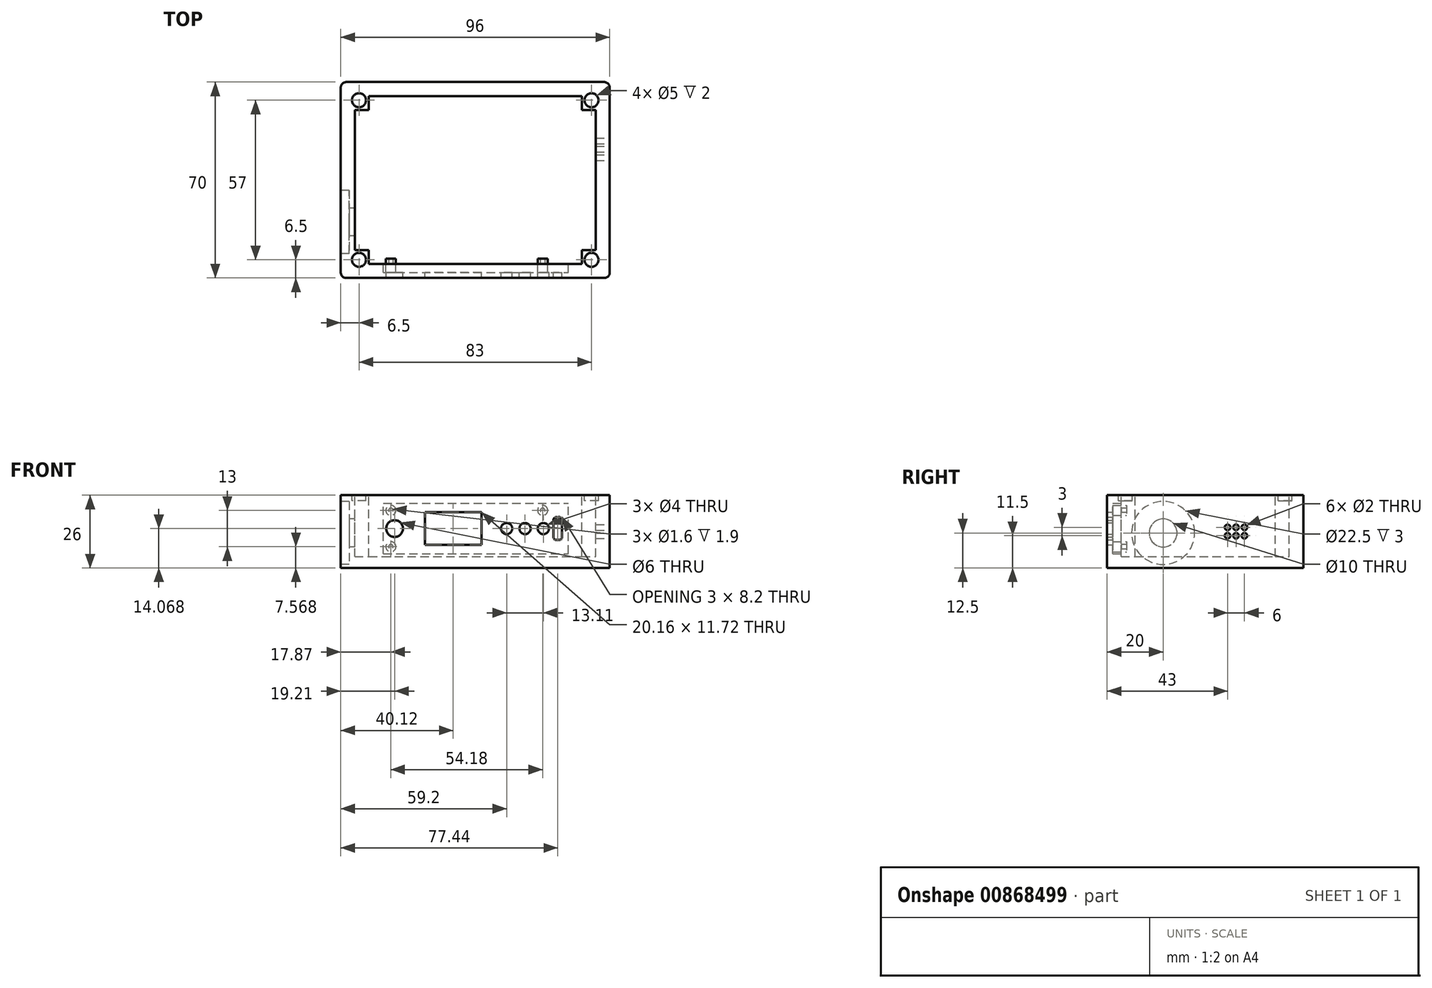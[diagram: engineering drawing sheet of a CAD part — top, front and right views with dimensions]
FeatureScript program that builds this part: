
annotation { "Feature Type Name" : "Feature", "Feature Type Description" : "" }
export const myFeature = defineFeature(function(context is Context, id is Id, definition is map)
    precondition{}
    {
        {
            var Q0;
            Q0=qCreatedBy(makeId("Top.planeOp"),FACE);
            var sketch = newSketch(context, id + "F0", { "sketchPlane" : qUnion([Q0])});
            skLineSegment(sketch, "E0.bottom", {"start": v(-46, 35) * mm, "end": v(46, 35) * mm});
            skLineSegment(sketch, "E0.top", {"start": v(-46, -35) * mm, "end": v(46, -35) * mm});
            skLineSegment(sketch, "E0.left", {"start": v(-48, 33) * mm, "end": v(-48, -33) * mm});
            skLineSegment(sketch, "E0.right", {"start": v(48, 33) * mm, "end": v(48, -33) * mm});
            skPoint(sketch, "E0.middle", {"position": v(0, 0) * mm});
            skPoint(sketch, "E1.visualSharp", {"position": v(-48, 35) * mm});
            skArc(sketch, "E1.filletArc", {"start": v(-46, 35) * mm, "mid": v(-47.41, 34.41) * mm, "end": v(-48, 33) * mm});
            skPoint(sketch, "E2.visualSharp", {"position": v(-48, -35) * mm});
            skArc(sketch, "E2.filletArc", {"start": v(-48, -33) * mm, "mid": v(-47.41, -34.41) * mm, "end": v(-46, -35) * mm});
            skPoint(sketch, "E3.visualSharp", {"position": v(48, -35) * mm});
            skArc(sketch, "E3.filletArc", {"start": v(46, -35) * mm, "mid": v(47.41, -34.41) * mm, "end": v(48, -33) * mm});
            skPoint(sketch, "E4.visualSharp", {"position": v(48, 35) * mm});
            skArc(sketch, "E4.filletArc", {"start": v(48, 33) * mm, "mid": v(47.41, 34.41) * mm, "end": v(46, 35) * mm});
            skSolve(sketch);
        }
        {
            var Q0;
            Q0=makeQuery(id+"F0.imprint","IMPRINT",FACE,{"disambiguationData":[TD([[makeQuery(id+"F0.imprint","IMPRINT",EDGE,{"derivedFrom":sQuery(id+"F0.wireOp",EDGE,"U18dfylj-Norm-gyCY-oxJm-QVkYRqjWbd2D.bottom")}),-1.0]])]});
            var Q1;
            Q1=qSketchRegion(id+"F0",true);
            extrude(context, id + "F1", {"entities" : qUnion([Q0, Q1]), "depth" : 26 * mm, "offsetDistance" : 25 * mm});
        }
        {
            var Q0;
            Q0=makeQuery(id+"F1.opExtrude","CAP_FACE",FACE,{"disambiguationData":[OSD([sQuery(id+"F0.wireOp",EDGE,"E0.bottom"),sQuery(id+"F0.wireOp",EDGE,"E0.top"),sQuery(id+"F0.wireOp",EDGE,"E0.left"),sQuery(id+"F0.wireOp",EDGE,"E0.right"),sQuery(id+"F0.wireOp",EDGE,"E1.filletArc"),sQuery(id+"F0.wireOp",EDGE,"E2.filletArc"),sQuery(id+"F0.wireOp",EDGE,"E3.filletArc"),sQuery(id+"F0.wireOp",EDGE,"E4.filletArc")])],"isStart":false});
            var sketch = newSketch(context, id + "F2", { "sketchPlane" : qUnion([Q0])});
            skLineSegment(sketch, "E5.bottom", {"start": v(-44.5, 33) * mm, "end": v(44.5, 33) * mm});
            skLineSegment(sketch, "E5.top", {"start": v(-44.5, -33) * mm, "end": v(44.5, -33) * mm});
            skLineSegment(sketch, "E5.left", {"start": v(-46, 31.5) * mm, "end": v(-46, -31.5) * mm});
            skLineSegment(sketch, "E5.right", {"start": v(46, 31.5) * mm, "end": v(46, -31.5) * mm});
            skPoint(sketch, "E5.middle", {"position": v(0, 0) * mm});
            skPoint(sketch, "E6.visualSharp", {"position": v(-46, 33) * mm});
            skArc(sketch, "E6.filletArc", {"start": v(-44.5, 33) * mm, "mid": v(-45.56, 32.56) * mm, "end": v(-46, 31.5) * mm});
            skPoint(sketch, "E7.visualSharp", {"position": v(46, 33) * mm});
            skArc(sketch, "E7.filletArc", {"start": v(46, 31.5) * mm, "mid": v(45.56, 32.56) * mm, "end": v(44.5, 33) * mm});
            skPoint(sketch, "E8.visualSharp", {"position": v(46, -33) * mm});
            skArc(sketch, "E8.filletArc", {"start": v(44.5, -33) * mm, "mid": v(45.56, -32.56) * mm, "end": v(46, -31.5) * mm});
            skPoint(sketch, "E9.visualSharp", {"position": v(-46, -33) * mm});
            skArc(sketch, "E9.filletArc", {"start": v(-46, -31.5) * mm, "mid": v(-45.56, -32.56) * mm, "end": v(-44.5, -33) * mm});
            skLineSegment(sketch, "E10.bottom", {"start": v(-44, 31.5) * mm, "end": v(44, 31.5) * mm});
            skLineSegment(sketch, "E10.top", {"start": v(-44, -31.5) * mm, "end": v(44, -31.5) * mm});
            skLineSegment(sketch, "E10.left", {"start": v(-44.5, 31) * mm, "end": v(-44.5, -31) * mm});
            skLineSegment(sketch, "E10.right", {"start": v(44.5, 31) * mm, "end": v(44.5, -31) * mm});
            skArc(sketch, "E11.filletArc", {"start": v(-44, 31.5) * mm, "mid": v(-44.35, 31.35) * mm, "end": v(-44.5, 31) * mm});
            skArc(sketch, "E12.filletArc", {"start": v(-44.5, -31) * mm, "mid": v(-44.35, -31.35) * mm, "end": v(-44, -31.5) * mm});
            skArc(sketch, "E13.filletArc", {"start": v(44, -31.5) * mm, "mid": v(44.35, -31.35) * mm, "end": v(44.5, -31) * mm});
            skArc(sketch, "E14.filletArc", {"start": v(44.5, 31) * mm, "mid": v(44.35, 31.35) * mm, "end": v(44, 31.5) * mm});
            skSolve(sketch);
        }
        {
            var Q0;
            Q0=makeQuery(id+"FVReVV0em28uw1l_1.boolean.opBoolean","SPLIT",FACE,{"disambiguationData":[TD([makeQuery(id+"FVReVV0em28uw1l_1.opExtrude","SWEPT_FACE",FACE,{"disambiguationData":[OSD([sQuery(id+"F2.wireOp",EDGE,"E10.bottom")])]})])],"derivedFrom":makeQuery(id+"F1.opExtrude","CAP_FACE",FACE,{"disambiguationData":[OSD([sQuery(id+"F0.wireOp",EDGE,"E0.bottom"),sQuery(id+"F0.wireOp",EDGE,"E0.top"),sQuery(id+"F0.wireOp",EDGE,"E0.left"),sQuery(id+"F0.wireOp",EDGE,"E0.right"),sQuery(id+"F0.wireOp",EDGE,"E1.filletArc"),sQuery(id+"F0.wireOp",EDGE,"E2.filletArc"),sQuery(id+"F0.wireOp",EDGE,"E3.filletArc"),sQuery(id+"F0.wireOp",EDGE,"E4.filletArc")])],"isStart":false})});
            var sketch = newSketch(context, id + "F3", { "sketchPlane" : qUnion([Q0])});
            skCircle(sketch, "E15", {"center": v(-41.5, -28.5) * mm, "radius": 2.5 * mm});
            skCircle(sketch, "E16", {"center": v(-41.5, 28.5) * mm, "radius": 2.5 * mm});
            skCircle(sketch, "E17", {"center": v(41.5, 28.5) * mm, "radius": 2.5 * mm});
            skCircle(sketch, "E18", {"center": v(41.5, -28.5) * mm, "radius": 2.5 * mm});
            skSolve(sketch);
        }
        {
            var Q0;
            Q0=makeQuery(id+"F3.imprint","IMPRINT",FACE,{"disambiguationData":[TD([[makeQuery(id+"F3.imprint","IMPRINT",EDGE,{"derivedFrom":sQuery(id+"F3.wireOp",EDGE,"E15")}),1.0]])]});
            var Q1;
            Q1=makeQuery(id+"F3.imprint","IMPRINT",FACE,{"disambiguationData":[TD([[makeQuery(id+"F3.imprint","IMPRINT",EDGE,{"derivedFrom":sQuery(id+"F3.wireOp",EDGE,"E16")}),1.0]])]});
            var Q2;
            Q2=makeQuery(id+"F3.imprint","IMPRINT",FACE,{"disambiguationData":[TD([[makeQuery(id+"F3.imprint","IMPRINT",EDGE,{"derivedFrom":sQuery(id+"F3.wireOp",EDGE,"E17")}),1.0]])]});
            var Q3;
            Q3=makeQuery(id+"F3.imprint","IMPRINT",FACE,{"disambiguationData":[TD([[makeQuery(id+"F3.imprint","IMPRINT",EDGE,{"derivedFrom":sQuery(id+"F3.wireOp",EDGE,"E18")}),1.0]])]});
            extrude(context, id + "F4", {"entities" : qUnion([Q0, Q1, Q2, Q3]), "operationType" : NewBodyOperationType.REMOVE, "oppositeDirection" : true, "depth" : 2 * mm, "offsetDistance" : 25 * mm});
        }
        {
            var Q0;
            Q0=makeQuery(id+"FVReVV0em28uw1l_1.boolean.opBoolean","SPLIT",FACE,{"disambiguationData":[TD([makeQuery(id+"FVReVV0em28uw1l_1.opExtrude","SWEPT_FACE",FACE,{"disambiguationData":[OSD([sQuery(id+"F2.wireOp",EDGE,"E10.bottom")])]})])],"derivedFrom":makeQuery(id+"F1.opExtrude","CAP_FACE",FACE,{"disambiguationData":[OSD([sQuery(id+"F0.wireOp",EDGE,"E0.bottom"),sQuery(id+"F0.wireOp",EDGE,"E0.top"),sQuery(id+"F0.wireOp",EDGE,"E0.left"),sQuery(id+"F0.wireOp",EDGE,"E0.right"),sQuery(id+"F0.wireOp",EDGE,"E1.filletArc"),sQuery(id+"F0.wireOp",EDGE,"E2.filletArc"),sQuery(id+"F0.wireOp",EDGE,"E3.filletArc"),sQuery(id+"F0.wireOp",EDGE,"E4.filletArc")])],"isStart":false})});
            var sketch = newSketch(context, id + "F5", { "sketchPlane" : qUnion([Q0])});
            skLineSegment(sketch, "E19.bottom", {"start": v(-43, -25) * mm, "end": v(43, -25) * mm});
            skLineSegment(sketch, "E19.top", {"start": v(-43, 25) * mm, "end": v(43, 25) * mm});
            skLineSegment(sketch, "E19.left", {"start": v(-43, -25) * mm, "end": v(-43, 25) * mm});
            skLineSegment(sketch, "E19.right", {"start": v(43, -25) * mm, "end": v(43, 25) * mm});
            skPoint(sketch, "E19.middle", {"position": v(0, 0) * mm});
            skLineSegment(sketch, "E20.bottom", {"start": v(-38, -30) * mm, "end": v(38, -30) * mm});
            skLineSegment(sketch, "E20.top", {"start": v(-38, 30) * mm, "end": v(38, 30) * mm});
            skLineSegment(sketch, "E20.left", {"start": v(-38, -30) * mm, "end": v(-38, 30) * mm});
            skLineSegment(sketch, "E20.right", {"start": v(38, -30) * mm, "end": v(38, 30) * mm});
            skSolve(sketch);
        }
        {
            var Q0;
            {var subQ0=sQuery(id+"F5.wireOp",EDGE,"E19.left");Q0=makeQuery(id+"F5.imprint","IMPRINT",FACE,{"disambiguationData":[TD([[makeQuery(id+"F5.imprint","IMPRINT",EDGE,{"derivedFrom":subQ0}),-1.0]])]});}
            var Q1;
            {var subQ5=sQuery(id+"F5.wireOp",EDGE,"E20.bottom");Q1=makeQuery(id+"F5.imprint","IMPRINT",FACE,{"disambiguationData":[TD([[makeQuery(id+"F5.imprint","IMPRINT",EDGE,{"derivedFrom":subQ5}),1.0]])]});}
            var Q2;
            {var subQ0=sQuery(id+"F5.wireOp",EDGE,"E20.left");var subQ1=sQuery(id+"F5.wireOp",EDGE,"E19.bottom");var subQ2=makeQuery(id+"F5.imprint","INTERSECT",VERTEX,{"derivedFrom":[subQ1,subQ0]});Q2=makeQuery(id+"F5.imprint","IMPRINT",FACE,{"disambiguationData":[TD([[makeQuery(id+"F5.imprint","IMPRINT",EDGE,{"disambiguationData":[TD([[subQ2,-1.0]])],"derivedFrom":subQ1}),1.0]])]});}
            var Q3;
            {var subQ5=sQuery(id+"F5.wireOp",EDGE,"E20.top");Q3=makeQuery(id+"F5.imprint","IMPRINT",FACE,{"disambiguationData":[TD([[makeQuery(id+"F5.imprint","IMPRINT",EDGE,{"derivedFrom":subQ5}),-1.0]])]});}
            var Q4;
            {var subQ0=sQuery(id+"F5.wireOp",EDGE,"E19.right");Q4=makeQuery(id+"F5.imprint","IMPRINT",FACE,{"disambiguationData":[TD([[makeQuery(id+"F5.imprint","IMPRINT",EDGE,{"derivedFrom":subQ0}),1.0]])]});}
            extrude(context, id + "F6", {"entities" : qUnion([Q0, Q1, Q2, Q3, Q4]), "operationType" : NewBodyOperationType.REMOVE, "oppositeDirection" : true, "depth" : 22 * mm, "offsetDistance" : 25 * mm});
        }
        {
            var Q0;
            Q0=makeQuery(id+"F1.opExtrude","SWEPT_FACE",FACE,{"disambiguationData":[OSD([sQuery(id+"F0.wireOp",EDGE,"E0.right")])]});
            var sketch = newSketch(context, id + "F7", { "sketchPlane" : qUnion([Q0])});
            skPoint(sketch, "E21.centerSnap0", {"position": v(-33, 13) * mm});
            skCircle(sketch, "E22", {"center": v(8, 14.5) * mm, "radius": 1 * mm});
            skPoint(sketch, "E22.centerSnap0", {"position": v(0, 0) * mm});
            skCircle(sketch, "E23", {"center": v(11, 14.5) * mm, "radius": 1 * mm});
            skCircle(sketch, "E24", {"center": v(14, 14.5) * mm, "radius": 1 * mm});
            skCircle(sketch, "E25", {"center": v(8, 11.5) * mm, "radius": 1 * mm});
            skCircle(sketch, "E26", {"center": v(11, 11.5) * mm, "radius": 1 * mm});
            skCircle(sketch, "E27", {"center": v(14, 11.5) * mm, "radius": 1 * mm});
            skSolve(sketch);
        }
        {
            var Q0;
            Q0=makeQuery(id+"F7.imprint","IMPRINT",FACE,{"disambiguationData":[TD([[makeQuery(id+"F7.imprint","IMPRINT",EDGE,{"derivedFrom":sQuery(id+"F7.wireOp",EDGE,"E22")}),1.0]])]});
            var Q1;
            Q1=makeQuery(id+"F7.imprint","IMPRINT",FACE,{"disambiguationData":[TD([[makeQuery(id+"F7.imprint","IMPRINT",EDGE,{"derivedFrom":sQuery(id+"F7.wireOp",EDGE,"E25")}),1.0]])]});
            var Q2;
            Q2=makeQuery(id+"F7.imprint","IMPRINT",FACE,{"disambiguationData":[TD([[makeQuery(id+"F7.imprint","IMPRINT",EDGE,{"derivedFrom":sQuery(id+"F7.wireOp",EDGE,"E26")}),1.0]])]});
            var Q3;
            Q3=makeQuery(id+"F7.imprint","IMPRINT",FACE,{"disambiguationData":[TD([[makeQuery(id+"F7.imprint","IMPRINT",EDGE,{"derivedFrom":sQuery(id+"F7.wireOp",EDGE,"E23")}),1.0]])]});
            var Q4;
            Q4=makeQuery(id+"F7.imprint","IMPRINT",FACE,{"disambiguationData":[TD([[makeQuery(id+"F7.imprint","IMPRINT",EDGE,{"derivedFrom":sQuery(id+"F7.wireOp",EDGE,"E24")}),1.0]])]});
            var Q5;
            Q5=makeQuery(id+"F7.imprint","IMPRINT",FACE,{"disambiguationData":[TD([[makeQuery(id+"F7.imprint","IMPRINT",EDGE,{"derivedFrom":sQuery(id+"F7.wireOp",EDGE,"E27")}),1.0]])]});
            extrude(context, id + "F8", {"entities" : qUnion([Q0, Q1, Q2, Q3, Q4, Q5]), "operationType" : NewBodyOperationType.REMOVE, "endBound" : BoundingType.UP_TO_NEXT, "oppositeDirection" : true, "depth" : 25 * mm, "offsetDistance" : 25 * mm});
        }
        {
            var Q0;
            Q0=makeQuery(id+"F1.opExtrude","SWEPT_FACE",FACE,{"disambiguationData":[OSD([sQuery(id+"F0.wireOp",EDGE,"E0.left")])]});
            var sketch = newSketch(context, id + "F9", { "sketchPlane" : qUnion([Q0])});
            skCircle(sketch, "E28", {"center": v(15, 12.5) * mm, "radius": 5 * mm});
            skCircle(sketch, "E29", {"center": v(15, 12.5) * mm, "radius": 11.25 * mm});
            skSolve(sketch);
        }
        {
            var Q0;
            Q0=makeQuery(id+"F9.imprint","IMPRINT",FACE,{"disambiguationData":[TD([[makeQuery(id+"F9.imprint","IMPRINT",EDGE,{"derivedFrom":sQuery(id+"F9.wireOp",EDGE,"E28")}),-1.0]])]});
            extrude(context, id + "F10", {"entities" : qUnion([Q0]), "operationType" : NewBodyOperationType.REMOVE, "oppositeDirection" : true, "depth" : 3 * mm, "offsetDistance" : 25 * mm});
        }
        {
            var Q0;
            Q0=makeQuery(id+"F9.imprint","IMPRINT",FACE,{"disambiguationData":[TD([[makeQuery(id+"F9.imprint","IMPRINT",EDGE,{"derivedFrom":sQuery(id+"F9.wireOp",EDGE,"E28")}),1.0]])]});
            extrude(context, id + "F11", {"entities" : qUnion([Q0]), "operationType" : NewBodyOperationType.REMOVE, "endBound" : BoundingType.UP_TO_NEXT, "oppositeDirection" : true, "depth" : 25 * mm, "offsetDistance" : 25 * mm});
        }
        {
            var Q0;
            Q0=makeQuery(id+"F6.boolean.opBoolean","COPY",FACE,{"derivedFrom":makeQuery(id+"F6.opExtrude","SWEPT_FACE",FACE,{"disambiguationData":[OSD([sQuery(id+"F5.wireOp",EDGE,"E20.bottom")])]})});
            var sketch = newSketch(context, id + "F12", { "sketchPlane" : qUnion([Q0])});
            skLineSegment(sketch, "E30.bottom", {"start": v(32.79, 5.07) * mm, "end": v(-33.21, 5.07) * mm});
            skLineSegment(sketch, "E30.top", {"start": v(32.79, 23.07) * mm, "end": v(-33.21, 23.07) * mm});
            skLineSegment(sketch, "E30.left", {"start": v(32.79, 5.07) * mm, "end": v(32.79, 23.07) * mm});
            skLineSegment(sketch, "E30.right", {"start": v(-33.21, 5.07) * mm, "end": v(-33.21, 23.07) * mm});
            skPoint(sketch, "E30.middle", {"position": v(-0.21, 14.07) * mm});
            skPoint(sketch, "E30.middle.positionSnap0", {"position": v(45.84, 14.07) * mm});
            skPoint(sketch, "E30.centerSnap0", {"position": v(45.84, 14.07) * mm});
            skLineSegment(sketch, "E31.bottom", {"start": v(-29.94, 9.97) * mm, "end": v(-28.94, 9.97) * mm});
            skLineSegment(sketch, "E31.top", {"start": v(-29.94, 18.17) * mm, "end": v(-28.94, 18.17) * mm});
            skLineSegment(sketch, "E31.left", {"start": v(-30.94, 10.97) * mm, "end": v(-30.94, 17.17) * mm});
            skLineSegment(sketch, "E31.right", {"start": v(-27.94, 10.97) * mm, "end": v(-27.94, 17.17) * mm});
            skPoint(sketch, "E31.middle", {"position": v(-29.44, 14.07) * mm});
            skPoint(sketch, "E31.middle.positionSnap0", {"position": v(-33.21, 14.07) * mm});
            skPoint(sketch, "E31.centerSnap0", {"position": v(-33.21, 14.07) * mm});
            skPoint(sketch, "E32.visualSharp", {"position": v(-27.94, 18.17) * mm});
            skArc(sketch, "E32.filletArc", {"start": v(-27.94, 17.17) * mm, "mid": v(-28.23, 17.87) * mm, "end": v(-28.94, 18.17) * mm});
            skPoint(sketch, "E33.visualSharp", {"position": v(-27.94, 9.97) * mm});
            skArc(sketch, "E33.filletArc", {"start": v(-28.94, 9.97) * mm, "mid": v(-28.23, 10.26) * mm, "end": v(-27.94, 10.97) * mm});
            skPoint(sketch, "E34.visualSharp", {"position": v(-30.94, 9.97) * mm});
            skArc(sketch, "E34.filletArc", {"start": v(-30.94, 10.97) * mm, "mid": v(-30.65, 10.26) * mm, "end": v(-29.94, 9.97) * mm});
            skPoint(sketch, "E35.visualSharp", {"position": v(-30.94, 18.17) * mm});
            skArc(sketch, "E35.filletArc", {"start": v(-29.94, 18.17) * mm, "mid": v(-30.65, 17.87) * mm, "end": v(-30.94, 17.17) * mm});
            skCircle(sketch, "E36", {"center": v(-24.31, 14.07) * mm, "radius": 2 * mm});
            skCircle(sketch, "E37", {"center": v(-17.76, 14.07) * mm, "radius": 2 * mm});
            skCircle(sketch, "E38", {"center": v(-11.2, 14.07) * mm, "radius": 2 * mm});
            skCircle(sketch, "E39", {"center": v(28.79, 14.07) * mm, "radius": 3 * mm});
            skCircle(sketch, "E40", {"center": v(30.13, 20.57) * mm, "radius": 1.8 * mm});
            skCircle(sketch, "E41", {"center": v(30.13, 20.57) * mm, "radius": 0.8 * mm});
            skCircle(sketch, "E42", {"center": v(30.13, 7.57) * mm, "radius": 1.8 * mm});
            skCircle(sketch, "E43", {"center": v(30.13, 7.57) * mm, "radius": 0.8 * mm});
            skLineSegment(sketch, "E44.bottom", {"start": v(-2.2, 19.93) * mm, "end": v(17.96, 19.93) * mm});
            skLineSegment(sketch, "E44.top", {"start": v(-2.2, 8.2) * mm, "end": v(17.96, 8.2) * mm});
            skLineSegment(sketch, "E44.left", {"start": v(-2.2, 19.93) * mm, "end": v(-2.2, 8.2) * mm});
            skLineSegment(sketch, "E44.right", {"start": v(17.96, 19.93) * mm, "end": v(17.96, 8.2) * mm});
            skPoint(sketch, "E44.middle", {"position": v(7.88, 14.07) * mm});
            skCircle(sketch, "E45", {"center": v(-24.05, 20.57) * mm, "radius": 1.8 * mm});
            skCircle(sketch, "E46", {"center": v(-24.05, 20.57) * mm, "radius": 0.8 * mm});
            skSolve(sketch);
        }
        {
            var Q0;
            Q0=makeQuery(id+"F12.imprint","IMPRINT",FACE,{"disambiguationData":[TD([[makeQuery(id+"F12.imprint","IMPRINT",EDGE,{"derivedFrom":sQuery(id+"F12.wireOp",EDGE,"E44.bottom")}),-1.0]])]});
            var Q1;
            Q1=makeQuery(id+"F12.imprint","IMPRINT",FACE,{"disambiguationData":[TD([[makeQuery(id+"F12.imprint","IMPRINT",EDGE,{"derivedFrom":sQuery(id+"F12.wireOp",EDGE,"E39")}),1.0]])]});
            var Q2;
            Q2=makeQuery(id+"F12.imprint","IMPRINT",FACE,{"disambiguationData":[TD([[makeQuery(id+"F12.imprint","IMPRINT",EDGE,{"derivedFrom":sQuery(id+"F12.wireOp",EDGE,"E38")}),1.0]])]});
            var Q3;
            Q3=makeQuery(id+"F12.imprint","IMPRINT",FACE,{"disambiguationData":[TD([[makeQuery(id+"F12.imprint","IMPRINT",EDGE,{"derivedFrom":sQuery(id+"F12.wireOp",EDGE,"E37")}),1.0]])]});
            var Q4;
            Q4=makeQuery(id+"F12.imprint","IMPRINT",FACE,{"disambiguationData":[TD([[makeQuery(id+"F12.imprint","IMPRINT",EDGE,{"derivedFrom":sQuery(id+"F12.wireOp",EDGE,"E36")}),1.0]])]});
            var Q5;
            Q5=makeQuery(id+"F12.imprint","IMPRINT",FACE,{"disambiguationData":[TD([[makeQuery(id+"F12.imprint","IMPRINT",EDGE,{"derivedFrom":sQuery(id+"F12.wireOp",EDGE,"E31.bottom")}),1.0]])]});
            extrude(context, id + "F13", {"entities" : qUnion([Q0, Q1, Q2, Q3, Q4, Q5]), "operationType" : NewBodyOperationType.REMOVE, "endBound" : BoundingType.UP_TO_NEXT, "oppositeDirection" : true, "depth" : 25 * mm, "offsetDistance" : 25 * mm});
        }
        {
            var Q0;
            Q0=makeQuery(id+"F12.imprint","IMPRINT",FACE,{"disambiguationData":[TD([[makeQuery(id+"F12.imprint","IMPRINT",EDGE,{"derivedFrom":sQuery(id+"F12.wireOp",EDGE,"E30.bottom")}),-1.0]])]});
            extrude(context, id + "F14", {"entities" : qUnion([Q0]), "operationType" : NewBodyOperationType.REMOVE, "oppositeDirection" : true, "depth" : -3 * mm, "offsetDistance" : 25 * mm});
        }
        {
            var Q0;
            Q0=makeQuery(id+"F12.imprint","IMPRINT",FACE,{"disambiguationData":[TD([[makeQuery(id+"F12.imprint","IMPRINT",EDGE,{"derivedFrom":sQuery(id+"F12.wireOp",EDGE,"E30.bottom")}),-1.0]])]});
            extrude(context, id + "F15", {"entities" : qUnion([Q0]), "operationType" : NewBodyOperationType.REMOVE, "oppositeDirection" : true, "depth" : 3 * mm, "offsetDistance" : 25 * mm});
        }
        {
            var Q0;
            Q0=makeQuery(id+"F12.imprint","IMPRINT",FACE,{"disambiguationData":[TD([[makeQuery(id+"F12.imprint","IMPRINT",EDGE,{"derivedFrom":sQuery(id+"F12.wireOp",EDGE,"E40")}),1.0]])]});
            var Q1;
            Q1=sQuery(id+"F12.wireOp",EDGE,"E41");
            var Q2;
            Q2=sQuery(id+"F12.wireOp",EDGE,"E40");
            extrude(context, id + "F16", {"entities" : qUnion([Q0]), "operationType" : NewBodyOperationType.ADD, "surfaceEntities" : qUnion([Q1, Q2]), "depth" : 1.9 * mm, "offsetDistance" : 25 * mm});
        }
        {
            var Q0;
            Q0=makeQuery(id+"F12.imprint","IMPRINT",FACE,{"disambiguationData":[TD([[makeQuery(id+"F12.imprint","IMPRINT",EDGE,{"derivedFrom":sQuery(id+"F12.wireOp",EDGE,"E42")}),1.0]])]});
            var Q1;
            Q1=sQuery(id+"F12.wireOp",EDGE,"E43");
            var Q2;
            Q2=sQuery(id+"F12.wireOp",EDGE,"E42");
            extrude(context, id + "F17", {"entities" : qUnion([Q0]), "operationType" : NewBodyOperationType.ADD, "surfaceEntities" : qUnion([Q1, Q2]), "depth" : 1.9 * mm, "offsetDistance" : 25 * mm});
        }
        {
            var Q0;
            Q0=makeQuery(id+"F12.imprint","IMPRINT",FACE,{"disambiguationData":[TD([[makeQuery(id+"F12.imprint","IMPRINT",EDGE,{"derivedFrom":sQuery(id+"F12.wireOp",EDGE,"E45")}),1.0]])]});
            extrude(context, id + "F18", {"entities" : qUnion([Q0]), "operationType" : NewBodyOperationType.ADD, "depth" : 1.9 * mm, "offsetDistance" : 25 * mm});
        }
    });
